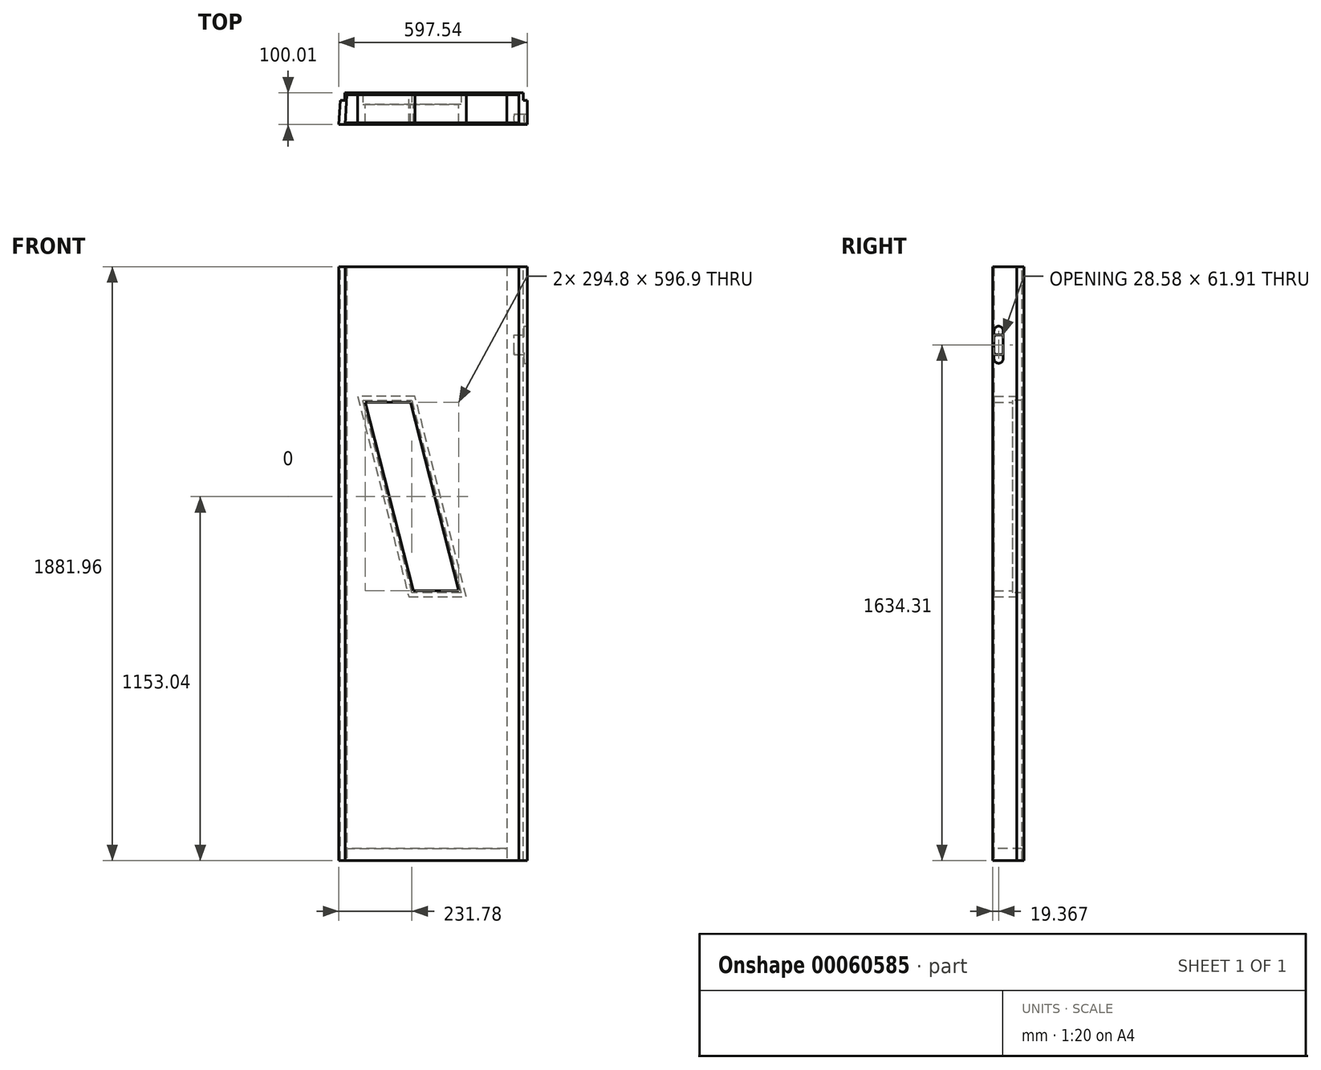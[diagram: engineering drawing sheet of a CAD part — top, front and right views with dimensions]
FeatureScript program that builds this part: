
annotation { "Feature Type Name" : "Feature", "Feature Type Description" : "" }
export const myFeature = defineFeature(function(context is Context, id is Id, definition is map)
    precondition{}
    {
        {
            var Q0;
            Q0=qCreatedBy(makeId("Front.planeOp"),FACE);
            var sketch = newSketch(context, id + "F0", { "sketchPlane" : qUnion([Q0])});
            skLineSegment(sketch, "E0.bottom", {"start": v(-27.3, 1881.96) * mm, "end": v(0, 1881.96) * mm});
            skLineSegment(sketch, "E0.top", {"start": v(-27.3, 0) * mm, "end": v(0, 0) * mm});
            skLineSegment(sketch, "E0.left", {"start": v(-27.3, 1881.96) * mm, "end": v(-27.3, 0) * mm});
            skLineSegment(sketch, "E0.right", {"start": v(0, 1881.96) * mm, "end": v(0, 0) * mm});
            skSolve(sketch);
        }
        {
            var Q0;
            Q0=makeQuery(id+"F0.imprint","IMPRINT",FACE,{"disambiguationData":[TD([[makeQuery(id+"F0.imprint","IMPRINT",EDGE,{"derivedFrom":sQuery(id+"F0.wireOp",EDGE,"E0.bottom")}),-1.0]])]});
            extrude(context, id + "F1", {"entities" : qUnion([Q0]), "oppositeDirection" : true, "depth" : 100.01 * mm});
        }
        {
            var Q0;
            Q0=makeQuery(id+"F1.opExtrude","SWEPT_FACE",FACE,{"disambiguationData":[OSD([sQuery(id+"F0.wireOp",EDGE,"E0.top")])]});
            var sketch = newSketch(context, id + "F2", { "sketchPlane" : qUnion([Q0])});
            skLineSegment(sketch, "E1.bottom", {"start": v(-27.3, -93.66) * mm, "end": v(-65.4, -93.66) * mm});
            skLineSegment(sketch, "E1.top", {"start": v(-27.3, -4.76) * mm, "end": v(-65.4, -4.76) * mm});
            skLineSegment(sketch, "E1.left", {"start": v(-27.3, -93.66) * mm, "end": v(-27.3, -4.76) * mm});
            skLineSegment(sketch, "E1.right", {"start": v(-65.4, -93.66) * mm, "end": v(-65.4, -4.76) * mm});
            skSolve(sketch);
        }
        {
            var Q0;
            Q0=makeQuery(id+"F2.imprint","IMPRINT",FACE,{"disambiguationData":[TD([[makeQuery(id+"F2.imprint","IMPRINT",EDGE,{"derivedFrom":sQuery(id+"F2.wireOp",EDGE,"E1.bottom")}),-1.0]])]});
            var Q1;
            Q1=makeQuery(id+"F1.opExtrude","SWEPT_FACE",FACE,{"disambiguationData":[OSD([sQuery(id+"F0.wireOp",EDGE,"E0.bottom")])]});
            extrude(context, id + "F3", {"entities" : qUnion([Q0]), "endBound" : BoundingType.UP_TO_SURFACE, "oppositeDirection" : true, "endBoundEntityFace" : qUnion([Q1]), "depth" : 25.4 * mm});
        }
        {
            var Q0;
            Q0=qCreatedBy(makeId("Right.planeOp"),FACE);
            cPlane(context, id + "F4", {"entities" : qUnion([Q0]), "cplaneType" : CPlaneType.OFFSET, "offset" : 600.7 * mm, "oppositeDirection" : true, "width" : 152.4 * mm, "height" : 152.4 * mm});
        }
        {
            var Q0;
            Q0=qCreatedBy(makeId("Top.planeOp"),FACE);
            var sketch = newSketch(context, id + "F5", { "sketchPlane" : qUnion([Q0])});
            skLineSegment(sketch, "E2", {"start": v(-591.48, 93.66) * mm, "end": v(-597.53, 0) * mm});
            skLineSegment(sketch, "E3", {"start": v(-597.53, 0) * mm, "end": v(-577.63, 0) * mm});
            skLineSegment(sketch, "E4", {"start": v(-577.63, 0) * mm, "end": v(-571.57, 93.66) * mm});
            skLineSegment(sketch, "E5", {"start": v(-597.53, 0) * mm, "end": v(-577.71, -1.28) * mm, "construction": true});
            skLineSegment(sketch, "E6", {"start": v(-591.48, 93.66) * mm, "end": v(-571.57, 93.66) * mm});
            skCircle(sketch, "E7", {"center": v(0, 0) * mm, "radius": 600.7 * mm, "construction": true});
            skSolve(sketch);
        }
        {
            var Q0;
            Q0=makeQuery(id+"F5.imprint","IMPRINT",FACE,{"disambiguationData":[TD([[makeQuery(id+"F5.imprint","IMPRINT",EDGE,{"derivedFrom":sQuery(id+"F5.wireOp",EDGE,"E2")}),1.0]])]});
            var Q1;
            Q1=makeQuery(id+"F1.opExtrude","SWEPT_FACE",FACE,{"disambiguationData":[OSD([sQuery(id+"F0.wireOp",EDGE,"E0.bottom")])]});
            extrude(context, id + "F6", {"entities" : qUnion([Q0]), "endBound" : BoundingType.UP_TO_SURFACE, "endBoundEntityFace" : qUnion([Q1]), "depth" : 25.4 * mm});
        }
        {
            var Q0;
            Q0=makeQuery(id+"F1.opExtrude","SWEPT_FACE",FACE,{"disambiguationData":[OSD([sQuery(id+"F0.wireOp",EDGE,"E0.top")])]});
            var sketch = newSketch(context, id + "F7", { "sketchPlane" : qUnion([Q0])});
            skLineSegment(sketch, "E8", {"start": v(-27.3, -4.76) * mm, "end": v(-577.32, -4.76) * mm});
            skLineSegment(sketch, "E9", {"start": v(-577.32, -4.76) * mm, "end": v(-577.63, 0) * mm});
            skLineSegment(sketch, "E10", {"start": v(-577.63, 0) * mm, "end": v(-27.3, 0) * mm});
            skLineSegment(sketch, "E11", {"start": v(-27.3, 0) * mm, "end": v(-27.3, -4.76) * mm});
            skSolve(sketch);
        }
        {
            var Q0;
            Q0=makeQuery(id+"F7.imprint","IMPRINT",FACE,{"disambiguationData":[TD([[makeQuery(id+"F7.imprint","IMPRINT",EDGE,{"derivedFrom":sQuery(id+"F7.wireOp",EDGE,"E8")}),-1.0]])]});
            var Q1;
            Q1=makeQuery(id+"F1.opExtrude","SWEPT_FACE",FACE,{"disambiguationData":[OSD([sQuery(id+"F0.wireOp",EDGE,"E0.bottom")])]});
            extrude(context, id + "F8", {"entities" : qUnion([Q0]), "endBound" : BoundingType.UP_TO_SURFACE, "oppositeDirection" : true, "endBoundEntityFace" : qUnion([Q1]), "depth" : 25.4 * mm});
        }
        {
            var Q0;
            Q0=makeQuery(id+"F3.opExtrude","CAP_FACE",FACE,{"disambiguationData":[OSD([sQuery(id+"F2.wireOp",EDGE,"E1.bottom"),sQuery(id+"F2.wireOp",EDGE,"E1.top"),sQuery(id+"F2.wireOp",EDGE,"E1.left"),sQuery(id+"F2.wireOp",EDGE,"E1.right")])],"isStart":true});
            var sketch = newSketch(context, id + "F9", { "sketchPlane" : qUnion([Q0])});
            skLineSegment(sketch, "E12.0", {"start": v(-65.4, -93.66) * mm, "end": v(-65.4, -4.76) * mm});
            skLineSegment(sketch, "E13", {"start": v(-65.4, -93.66) * mm, "end": v(-571.57, -93.66) * mm});
            skLineSegment(sketch, "E14", {"start": v(-571.57, -93.66) * mm, "end": v(-577.32, -4.76) * mm});
            skLineSegment(sketch, "E15", {"start": v(-577.32, -4.76) * mm, "end": v(-65.4, -4.76) * mm});
            skSolve(sketch);
        }
        {
            var Q0;
            Q0=makeQuery(id+"F9.imprint","IMPRINT",FACE,{"disambiguationData":[TD([[makeQuery(id+"F9.imprint","IMPRINT",EDGE,{"derivedFrom":sQuery(id+"F9.wireOp",EDGE,"E12.0")}),1.0]])]});
            extrude(context, id + "F10", {"entities" : qUnion([Q0]), "oppositeDirection" : true, "depth" : 38.1 * mm});
        }
        {
            var Q0;
            Q0=makeQuery(id+"F1.opExtrude","SWEPT_FACE",FACE,{"disambiguationData":[OSD([sQuery(id+"F0.wireOp",EDGE,"E0.right")])]});
            var sketch = newSketch(context, id + "F11", { "sketchPlane" : qUnion([Q0])});
            skLineSegment(sketch, "E16", {"start": v(5.08, 1589.86) * mm, "end": v(5.08, 1678.76) * mm});
            skArc(sketch, "E17", {"start": v(33.65, 1678.76) * mm, "mid": v(19.37, 1693.05) * mm, "end": v(5.08, 1678.76) * mm});
            skArc(sketch, "E18", {"start": v(5.08, 1589.86) * mm, "mid": v(19.37, 1575.57) * mm, "end": v(33.66, 1589.86) * mm});
            skLineSegment(sketch, "E19", {"start": v(33.65, 1589.86) * mm, "end": v(33.65, 1678.76) * mm});
            skSolve(sketch);
        }
        {
            var Q0;
            Q0=makeQuery(id+"F11.imprint","IMPRINT",FACE,{"disambiguationData":[TD([[makeQuery(id+"F11.imprint","IMPRINT",EDGE,{"derivedFrom":sQuery(id+"F11.wireOp",EDGE,"E16")}),-1.0]])]});
            extrude(context, id + "F12", {"entities" : qUnion([Q0]), "operationType" : NewBodyOperationType.REMOVE, "oppositeDirection" : true, "depth" : 11.1 * mm});
        }
        {
            var Q0;
            Q0=makeQuery(id+"F12.boolean.opBoolean","COPY",FACE,{"derivedFrom":makeQuery(id+"F12.opExtrude","CAP_FACE",FACE,{"disambiguationData":[OSD([sQuery(id+"F11.wireOp",EDGE,"E16"),sQuery(id+"F11.wireOp",EDGE,"E17"),sQuery(id+"F11.wireOp",EDGE,"E18"),sQuery(id+"F11.wireOp",EDGE,"E19")])],"isStart":false})});
            var sketch = newSketch(context, id + "F13", { "sketchPlane" : qUnion([Q0])});
            skLineSegment(sketch, "E20.bottom", {"start": v(11.43, 1665.27) * mm, "end": v(27.3, 1665.27) * mm});
            skLineSegment(sketch, "E20.top", {"start": v(11.43, 1603.36) * mm, "end": v(27.3, 1603.36) * mm});
            skLineSegment(sketch, "E20.left", {"start": v(5.08, 1658.92) * mm, "end": v(5.08, 1609.7) * mm});
            skLineSegment(sketch, "E20.right", {"start": v(33.65, 1658.92) * mm, "end": v(33.65, 1609.7) * mm});
            skLineSegment(sketch, "E21", {"start": v(33.65, 1634.31) * mm, "end": v(5.08, 1634.31) * mm, "construction": true});
            skPoint(sketch, "E22.visualSharp", {"position": v(33.65, 1665.27) * mm});
            skArc(sketch, "E22.filletArc", {"start": v(33.66, 1658.92) * mm, "mid": v(31.8, 1663.4) * mm, "end": v(27.3, 1665.27) * mm});
            skPoint(sketch, "E23.visualSharp", {"position": v(33.65, 1603.36) * mm});
            skArc(sketch, "E23.filletArc", {"start": v(27.3, 1603.36) * mm, "mid": v(31.8, 1605.22) * mm, "end": v(33.65, 1609.7) * mm});
            skPoint(sketch, "E24.visualSharp", {"position": v(5.08, 1665.27) * mm});
            skArc(sketch, "E24.filletArc", {"start": v(11.43, 1665.27) * mm, "mid": v(6.94, 1663.4) * mm, "end": v(5.08, 1658.92) * mm});
            skPoint(sketch, "E25.visualSharp", {"position": v(5.08, 1603.36) * mm});
            skArc(sketch, "E25.filletArc", {"start": v(5.08, 1609.7) * mm, "mid": v(6.94, 1605.22) * mm, "end": v(11.43, 1603.36) * mm});
            skSolve(sketch);
        }
        {
            var Q0;
            Q0=makeQuery(id+"F13.imprint","IMPRINT",FACE,{"disambiguationData":[TD([[makeQuery(id+"F13.imprint","IMPRINT",EDGE,{"derivedFrom":sQuery(id+"F13.wireOp",EDGE,"E20.bottom")}),-1.0]])]});
            extrude(context, id + "F14", {"entities" : qUnion([Q0]), "operationType" : NewBodyOperationType.REMOVE, "oppositeDirection" : true, "depth" : 30.96 * mm});
        }
        {
            var Q0;
            Q0=qCreatedBy(id+"F4.planeOp",FACE);
            var sketch = newSketch(context, id + "F15", { "sketchPlane" : qUnion([Q0])});
            skLineSegment(sketch, "E26", {"start": v(0, 1602.52) * mm, "end": v(0, 1246.92) * mm});
            skLineSegment(sketch, "E27", {"start": v(0, 1246.92) * mm, "end": v(-10.16, 1246.92) * mm});
            skLineSegment(sketch, "E28", {"start": v(-10.16, 1246.92) * mm, "end": v(0, 1602.52) * mm});
            skLineSegment(sketch, "E29", {"start": v(-6.17, 1386.62) * mm, "end": v(0, 1742.17) * mm});
            skLineSegment(sketch, "E30", {"start": v(0, 1742.17) * mm, "end": v(-16.33, 1386.8) * mm});
            skLineSegment(sketch, "E31", {"start": v(-16.33, 1386.8) * mm, "end": v(-6.17, 1386.62) * mm});
            skLineSegment(sketch, "E32", {"start": v(-9.9, 1526.5) * mm, "end": v(0, 1881.96) * mm});
            skLineSegment(sketch, "E33", {"start": v(0, 1881.96) * mm, "end": v(-20.06, 1526.78) * mm});
            skLineSegment(sketch, "E34", {"start": v(-20.06, 1526.78) * mm, "end": v(-9.9, 1526.5) * mm});
            skSolve(sketch);
        }
        {
            var Q0;
            Q0 = qSketchRegion(id + "F15", true);
            extrude(context, id + "F16", {"entities" : qUnion([Q0]), "depth" : 596.44 * mm});
        }
        {
            var Q0;
            Q0=makeQuery(id+"F1.opExtrude","SWEPT_FACE",FACE,{"disambiguationData":[OSD([sQuery(id+"F0.wireOp",EDGE,"E0.bottom")])]});
            var sketch = newSketch(context, id + "F17", { "sketchPlane" : qUnion([Q0])});
            skLineSegment(sketch, "E35.bottom", {"start": v(0, 100.01) * mm, "end": v(-12.7, 100.01) * mm});
            skLineSegment(sketch, "E35.top", {"start": v(0, 76.2) * mm, "end": v(-12.7, 76.2) * mm});
            skLineSegment(sketch, "E35.left", {"start": v(0, 100.01) * mm, "end": v(0, 76.2) * mm});
            skLineSegment(sketch, "E35.right", {"start": v(-12.7, 100.01) * mm, "end": v(-12.7, 76.2) * mm});
            skLineSegment(sketch, "E36.bottom", {"start": v(-591.48, 76.2) * mm, "end": v(-578.78, 76.2) * mm});
            skLineSegment(sketch, "E36.top", {"start": v(-591.48, 93.66) * mm, "end": v(-578.78, 93.66) * mm});
            skLineSegment(sketch, "E36.left", {"start": v(-591.48, 76.2) * mm, "end": v(-591.48, 93.66) * mm, "construction": true});
            skLineSegment(sketch, "E36.right", {"start": v(-578.78, 76.2) * mm, "end": v(-578.78, 93.66) * mm});
            skLineSegment(sketch, "E37", {"start": v(-591.48, 76.2) * mm, "end": v(-592.6, 76.2) * mm});
            skLineSegment(sketch, "E38", {"start": v(-592.6, 76.2) * mm, "end": v(-591.48, 93.66) * mm});
            skSolve(sketch);
        }
        {
            var Q0;
            Q0 = qSketchRegion(id + "F17", true);
            extrude(context, id + "F18", {"entities" : qUnion([Q0]), "operationType" : NewBodyOperationType.REMOVE, "endBound" : BoundingType.THROUGH_ALL, "oppositeDirection" : true, "depth" : 25.4 * mm});
        }
        {
            var Q0;
            Q0=makeQuery(id+"F1.opExtrude","SWEPT_FACE",FACE,{"disambiguationData":[OSD([sQuery(id+"F0.wireOp",EDGE,"E0.bottom")])]});
            var sketch = newSketch(context, id + "F19", { "sketchPlane" : qUnion([Q0])});
            skLineSegment(sketch, "E39", {"start": v(-27.3, 93.66) * mm, "end": v(-27.3, 100.01) * mm});
            skLineSegment(sketch, "E40", {"start": v(-27.3, 100.01) * mm, "end": v(-578.78, 100.01) * mm});
            skLineSegment(sketch, "E41", {"start": v(-578.78, 100.01) * mm, "end": v(-578.78, 93.66) * mm});
            skLineSegment(sketch, "E42", {"start": v(-578.78, 93.66) * mm, "end": v(-27.3, 93.66) * mm});
            skSolve(sketch);
        }
        {
            var Q0;
            Q0=makeQuery(id+"F19.imprint","IMPRINT",FACE,{"disambiguationData":[TD([[makeQuery(id+"F19.imprint","IMPRINT",EDGE,{"derivedFrom":sQuery(id+"F19.wireOp",EDGE,"E39")}),-1.0]])]});
            var Q1;
            Q1=makeQuery(id+"F10.opExtrude","CAP_FACE",FACE,{"disambiguationData":[OSD([sQuery(id+"F9.wireOp",EDGE,"E12.0"),sQuery(id+"F9.wireOp",EDGE,"E13"),sQuery(id+"F9.wireOp",EDGE,"E14"),sQuery(id+"F9.wireOp",EDGE,"E15")])],"isStart":true});
            extrude(context, id + "F20", {"entities" : qUnion([Q0]), "endBound" : BoundingType.UP_TO_SURFACE, "oppositeDirection" : true, "endBoundEntityFace" : qUnion([Q1]), "depth" : 25.4 * mm});
        }
        {
            var Q0;
            Q0=makeQuery(id+"F16.opExtrude","SWEPT_BODY",BODY,{"disambiguationData":[OSD([sQuery(id+"F15.wireOp",EDGE,"E26"),sQuery(id+"F15.wireOp",EDGE,"E27"),sQuery(id+"F15.wireOp",EDGE,"E28")])]});
            var Q1;
            Q1=makeQuery(id+"F16.opExtrude","SWEPT_BODY",BODY,{"disambiguationData":[OSD([sQuery(id+"F15.wireOp",EDGE,"E29"),sQuery(id+"F15.wireOp",EDGE,"E30"),sQuery(id+"F15.wireOp",EDGE,"E31")])]});
            var Q2;
            Q2=makeQuery(id+"F16.opExtrude","SWEPT_BODY",BODY,{"disambiguationData":[OSD([sQuery(id+"F15.wireOp",EDGE,"E32"),sQuery(id+"F15.wireOp",EDGE,"E33"),sQuery(id+"F15.wireOp",EDGE,"E34")])]});
            deleteBodies(context, id + "F21", {"entities" : qUnion([Q0, Q1, Q2])});
        }
        {
            var Q0;
            Q0=makeQuery(id+"F20.opExtrude","SWEPT_FACE",FACE,{"disambiguationData":[OSD([sQuery(id+"F19.wireOp",EDGE,"E42")])]});
            var sketch = newSketch(context, id + "F22", { "sketchPlane" : qUnion([Q0])});
            skLineSegment(sketch, "E43", {"start": v(-508.63, 848.24) * mm, "end": v(231.3, 848.24) * mm, "construction": true});
            skLineSegment(sketch, "E44", {"start": v(-521.33, 1457.84) * mm, "end": v(-365.76, 848.24) * mm});
            skLineSegment(sketch, "E45", {"start": v(-365.76, 848.24) * mm, "end": v(-210.18, 848.24) * mm});
            skLineSegment(sketch, "E46", {"start": v(-210.18, 848.24) * mm, "end": v(-365.76, 1457.84) * mm});
            skLineSegment(sketch, "E47", {"start": v(-365.76, 1457.84) * mm, "end": v(-521.33, 1457.84) * mm});
            skLineSegment(sketch, "E48", {"start": v(-365.76, 1457.84) * mm, "end": v(-365.76, 1881.96) * mm});
            skLineSegment(sketch, "E49", {"start": v(-365.76, 848.24) * mm, "end": v(-365.76, 424.12) * mm});
            skLineSegment(sketch, "E50", {"start": v(-365.76, 424.12) * mm, "end": v(-365.76, 0) * mm});
            skSolve(sketch);
        }
        {
            var Q0;
            Q0 = qSketchRegion(id + "F22", true);
            extrude(context, id + "F23", {"entities" : qUnion([Q0]), "operationType" : NewBodyOperationType.REMOVE, "endBound" : BoundingType.THROUGH_ALL, "oppositeDirection" : true, "depth" : 25.4 * mm});
        }
        {
            var Q0;
            Q0=makeQuery(id+"F8.opExtrude","SWEPT_FACE",FACE,{"disambiguationData":[OSD([sQuery(id+"F7.wireOp",EDGE,"E10")])]});
            cPlane(context, id + "F24", {"entities" : qUnion([Q0]), "cplaneType" : CPlaneType.OFFSET, "offset" : 63.5 * mm, "oppositeDirection" : true, "width" : 152.4 * mm, "height" : 152.4 * mm});
        }
        {
            var Q0;
            Q0=qCreatedBy(id+"F24.planeOp",FACE);
            var sketch = newSketch(context, id + "F25", { "sketchPlane" : qUnion([Q0])});
            skLineSegment(sketch, "E51.0", {"start": v(-521.33, 1457.84) * mm, "end": v(-365.76, 1457.84) * mm});
            skLineSegment(sketch, "E51.1", {"start": v(-210.18, 848.24) * mm, "end": v(-365.76, 848.24) * mm});
            skLineSegment(sketch, "E51.2", {"start": v(-365.76, 848.24) * mm, "end": v(-521.34, 1457.84) * mm});
            skLineSegment(sketch, "E51.3", {"start": v(-365.76, 1457.84) * mm, "end": v(-210.19, 848.24) * mm});
            skLineSegment(sketch, "E52.0", {"start": v(-513.16, 1451.5) * mm, "end": v(-370.7, 1451.5) * mm});
            skLineSegment(sketch, "E52.1", {"start": v(-360.83, 854.6) * mm, "end": v(-513.16, 1451.5) * mm});
            skLineSegment(sketch, "E52.2", {"start": v(-218.36, 854.6) * mm, "end": v(-360.83, 854.6) * mm});
            skLineSegment(sketch, "E52.3", {"start": v(-370.7, 1451.5) * mm, "end": v(-218.36, 854.6) * mm});
            skLineSegment(sketch, "E53.0", {"start": v(-537.68, 1470.54) * mm, "end": v(-355.9, 1470.54) * mm});
            skLineSegment(sketch, "E53.1", {"start": v(-375.63, 835.54) * mm, "end": v(-537.68, 1470.54) * mm});
            skLineSegment(sketch, "E53.2", {"start": v(-193.84, 835.54) * mm, "end": v(-375.63, 835.54) * mm});
            skLineSegment(sketch, "E53.3", {"start": v(-355.9, 1470.54) * mm, "end": v(-193.84, 835.54) * mm});
            skSolve(sketch);
        }
        {
            var Q0;
            Q0=makeQuery(id+"F25.imprint","IMPRINT",FACE,{"disambiguationData":[TD([[makeQuery(id+"F25.imprint","IMPRINT",EDGE,{"derivedFrom":sQuery(id+"F25.wireOp",EDGE,"E51.0")}),1.0]])]});
            var Q1;
            Q1=makeQuery(id+"F25.imprint","IMPRINT",FACE,{"disambiguationData":[TD([[makeQuery(id+"F25.imprint","IMPRINT",EDGE,{"derivedFrom":sQuery(id+"F25.wireOp",EDGE,"E51.0")}),-1.0]])]});
            var Q2;
            Q2=makeQuery(id+"F8.opExtrude","SWEPT_FACE",FACE,{"disambiguationData":[OSD([sQuery(id+"F7.wireOp",EDGE,"E8")])]});
            extrude(context, id + "F26", {"entities" : qUnion([Q0, Q1]), "endBound" : BoundingType.UP_TO_SURFACE, "endBoundEntityFace" : qUnion([Q2]), "depth" : 25.4 * mm});
        }
        {
            var Q0;
            Q0=makeQuery(id+"F25.imprint","IMPRINT",FACE,{"disambiguationData":[TD([[makeQuery(id+"F25.imprint","IMPRINT",EDGE,{"derivedFrom":sQuery(id+"F25.wireOp",EDGE,"E51.0")}),1.0]])]});
            var Q1;
            Q1=makeQuery(id+"F20.opExtrude","SWEPT_FACE",FACE,{"disambiguationData":[OSD([sQuery(id+"F19.wireOp",EDGE,"E42")])]});
            extrude(context, id + "F27", {"entities" : qUnion([Q0]), "operationType" : NewBodyOperationType.ADD, "endBound" : BoundingType.UP_TO_SURFACE, "oppositeDirection" : true, "endBoundEntityFace" : qUnion([Q1]), "depth" : 25.4 * mm});
        }
        {
            var Q0;
            Q0=makeQuery(id+"F25.imprint","IMPRINT",FACE,{"disambiguationData":[TD([[makeQuery(id+"F25.imprint","IMPRINT",EDGE,{"derivedFrom":sQuery(id+"F25.wireOp",EDGE,"E52.0")}),-1.0]])]});
            extrude(context, id + "F28", {"entities" : qUnion([Q0]), "operationType" : NewBodyOperationType.REMOVE, "endBound" : BoundingType.THROUGH_ALL, "depth" : 25.4 * mm});
        }
    });
